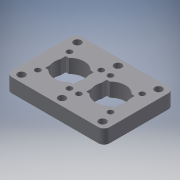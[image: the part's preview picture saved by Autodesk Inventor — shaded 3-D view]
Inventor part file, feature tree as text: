
AUTODESK INVENTOR PART (.ipt)
format: ipt  version: 2016 (Build 200138000, 138)  size: 191,488 bytes
history: native  units: mm
features: extrude x3, sketch x3, fillet x1
ambient origin geometry x8: Origin, YZ Plane, XZ Plane, XY Plane, X Axis, Y Axis, Z Axis, Center Point
bodies: Solid1 (feature_tree)
feature tree (7):
  extrude  "Extrusion1"  Depth=44.0mm
  fillet  "Fillet1"  Radius=44.0mm
  extrude  "Extrusion2"  Depth=8.0mm
  extrude  "Extrusion3"  Depth=75.0mm
  sketch  "Sketch1"  dims[d0=60.0mm d1=87.0mm d2=44.0mm]
  sketch  "Sketch2"  dims[d3=32.0mm d4=8.0mm]
  sketch  "Sketch3"  dims[d5=105.0mm d6=75.0mm d7=15.0mm d8=0.0mm d9=6.0mm d10=34.0mm d11=6.0mm d12=22.0mm d13=30.0mm d14=10.0mm d15=0.0mm d16=8.0mm d17=10.0mm d18=0.0mm]
